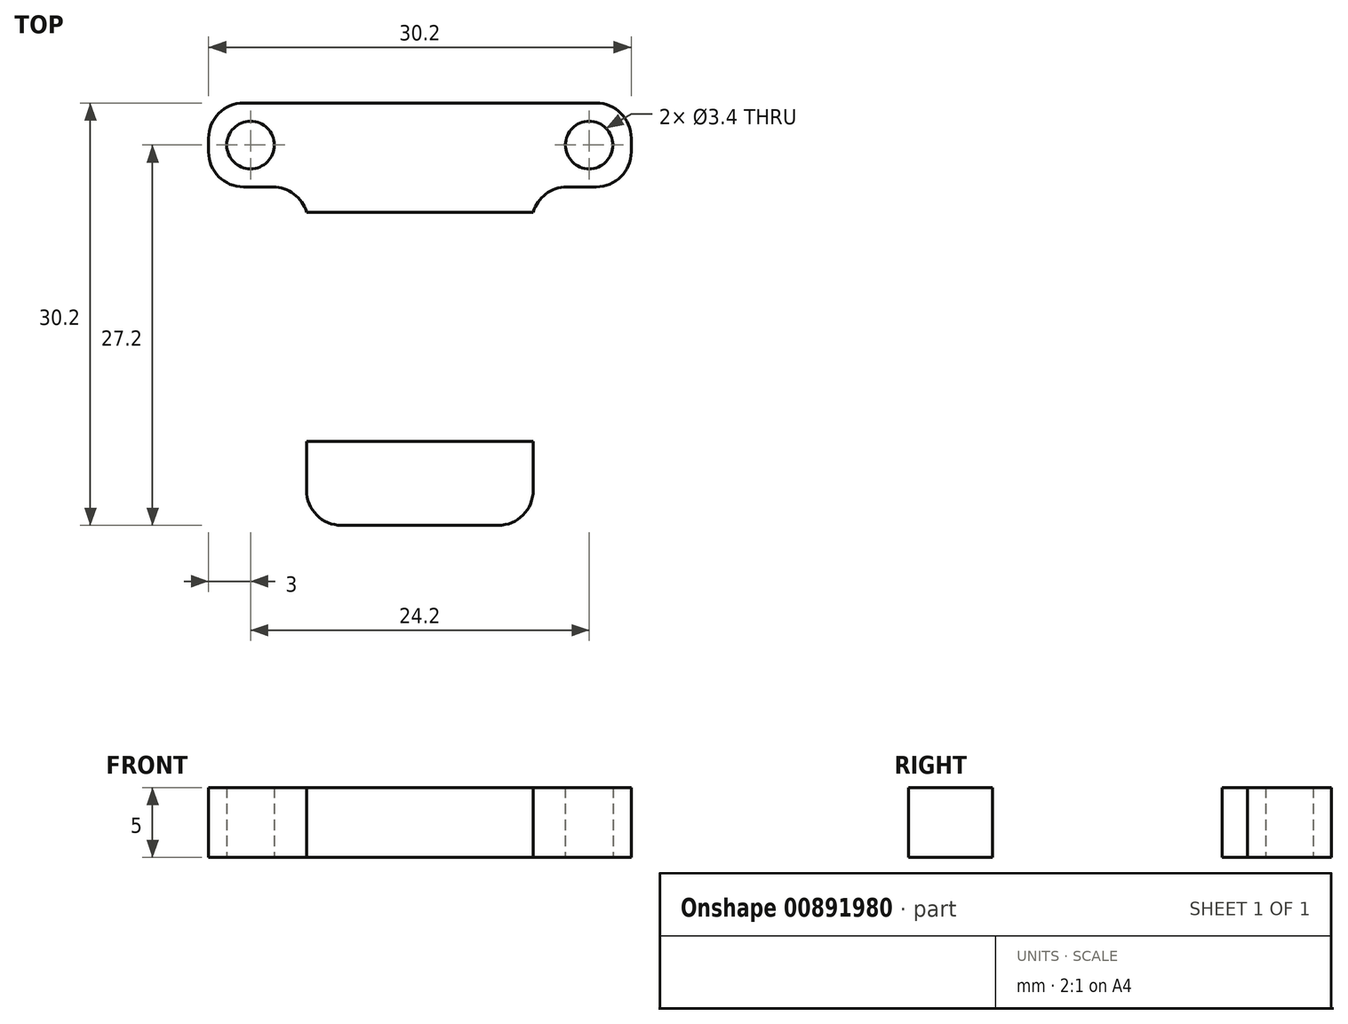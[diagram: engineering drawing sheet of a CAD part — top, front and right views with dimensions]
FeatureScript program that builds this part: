
annotation { "Feature Type Name" : "Feature", "Feature Type Description" : "" }
export const myFeature = defineFeature(function(context is Context, id is Id, definition is map)
    precondition{}
    {
        {
            var Q0;
            Q0=qCreatedBy(makeId("Top.planeOp"),FACE);
            var sketch = newSketch(context, id + "F0", { "sketchPlane" : qUnion([Q0])});
            skLineSegment(sketch, "E0.bottom", {"start": v(-15.1, -15.1) * mm, "end": v(15.1, -15.1) * mm});
            skLineSegment(sketch, "E0.top", {"start": v(-15.1, 15.1) * mm, "end": v(15.1, 15.1) * mm});
            skLineSegment(sketch, "E0.left", {"start": v(-15.1, -15.1) * mm, "end": v(-15.1, 15.1) * mm});
            skLineSegment(sketch, "E0.right", {"start": v(15.1, -15.1) * mm, "end": v(15.1, 15.1) * mm});
            skPoint(sketch, "E0.middle", {"position": v(0, 0) * mm});
            skLineSegment(sketch, "E1.bottom", {"start": v(-15.1, 15.1) * mm, "end": v(-12.1, 15.1) * mm});
            skLineSegment(sketch, "E1.top", {"start": v(-15.1, 12.1) * mm, "end": v(-12.1, 12.1) * mm, "construction": true});
            skLineSegment(sketch, "E1.left", {"start": v(-15.1, 15.1) * mm, "end": v(-15.1, 12.1) * mm});
            skLineSegment(sketch, "E1.right", {"start": v(-12.1, 15.1) * mm, "end": v(-12.1, 12.1) * mm, "construction": true});
            skLineSegment(sketch, "E2.1.0", {"start": v(-15.1, -12.1) * mm, "end": v(-12.1, -12.1) * mm, "construction": true});
            skLineSegment(sketch, "E2.1.1", {"start": v(-12.1, -15.1) * mm, "end": v(-12.1, -12.1) * mm, "construction": true});
            skLineSegment(sketch, "E2.1.2", {"start": v(-15.1, -15.1) * mm, "end": v(-15.1, -12.1) * mm});
            skLineSegment(sketch, "E2.2.0", {"start": v(12.1, -15.1) * mm, "end": v(12.1, -12.1) * mm, "construction": true});
            skLineSegment(sketch, "E2.2.1", {"start": v(15.1, -12.1) * mm, "end": v(12.1, -12.1) * mm, "construction": true});
            skLineSegment(sketch, "E2.2.2", {"start": v(15.1, -15.1) * mm, "end": v(12.1, -15.1) * mm});
            skLineSegment(sketch, "E2.3.0", {"start": v(15.1, 12.1) * mm, "end": v(12.1, 12.1) * mm, "construction": true});
            skLineSegment(sketch, "E2.3.1", {"start": v(12.1, 15.1) * mm, "end": v(12.1, 12.1) * mm, "construction": true});
            skLineSegment(sketch, "E2.3.2", {"start": v(15.1, 15.1) * mm, "end": v(15.1, 12.1) * mm});
            skLineSegment(sketch, "E3.bottom", {"start": v(-15.1, 15.1) * mm, "end": v(-9.1, 15.1) * mm});
            skLineSegment(sketch, "E3.top", {"start": v(-15.1, 9.1) * mm, "end": v(-9.1, 9.1) * mm, "construction": true});
            skLineSegment(sketch, "E3.left", {"start": v(-15.1, 15.1) * mm, "end": v(-15.1, 9.1) * mm});
            skLineSegment(sketch, "E3.right", {"start": v(-9.1, 15.1) * mm, "end": v(-9.1, 9.1) * mm, "construction": true});
            skLineSegment(sketch, "E4.1.0", {"start": v(-9.1, -15.1) * mm, "end": v(-9.1, -9.1) * mm, "construction": true});
            skLineSegment(sketch, "E4.1.1", {"start": v(-15.1, -9.1) * mm, "end": v(-9.1, -9.1) * mm, "construction": true});
            skLineSegment(sketch, "E4.2.0", {"start": v(15.1, -9.1) * mm, "end": v(9.1, -9.1) * mm, "construction": true});
            skLineSegment(sketch, "E4.2.1", {"start": v(9.1, -15.1) * mm, "end": v(9.1, -9.1) * mm, "construction": true});
            skLineSegment(sketch, "E4.3.0", {"start": v(9.1, 15.1) * mm, "end": v(9.1, 9.1) * mm, "construction": true});
            skLineSegment(sketch, "E4.3.1", {"start": v(15.1, 9.1) * mm, "end": v(9.1, 9.1) * mm, "construction": true});
            skLineSegment(sketch, "E5.bottom", {"start": v(-9.1, -9.1) * mm, "end": v(9.1, -9.1) * mm});
            skLineSegment(sketch, "E5.top", {"start": v(-9.1, 9.1) * mm, "end": v(9.1, 9.1) * mm});
            skLineSegment(sketch, "E5.left", {"start": v(-9.1, -9.1) * mm, "end": v(-9.1, 9.1) * mm});
            skLineSegment(sketch, "E5.right", {"start": v(9.1, -9.1) * mm, "end": v(9.1, 9.1) * mm});
            skLineSegment(sketch, "E6.bottom", {"start": v(-8.1, -15.1) * mm, "end": v(8.1, -15.1) * mm});
            skLineSegment(sketch, "E6.top", {"start": v(-8.1, -15.1) * mm, "end": v(8.1, -15.1) * mm});
            skLineSegment(sketch, "E6.left", {"start": v(-8.1, -15.1) * mm, "end": v(-8.1, -15.1) * mm});
            skLineSegment(sketch, "E6.right", {"start": v(8.1, -15.1) * mm, "end": v(8.1, -15.1) * mm});
            skPoint(sketch, "E6.middle", {"position": v(0, -15.1) * mm});
            skLineSegment(sketch, "E7.bottom", {"start": v(8.1, -15.1) * mm, "end": v(-8.1, -15.1) * mm});
            skLineSegment(sketch, "E7.top", {"start": v(8.1, 7.3) * mm, "end": v(-8.1, 7.3) * mm});
            skLineSegment(sketch, "E7.left", {"start": v(8.1, -15.1) * mm, "end": v(8.1, 7.3) * mm});
            skLineSegment(sketch, "E7.right", {"start": v(-8.1, -15.1) * mm, "end": v(-8.1, 7.3) * mm});
            skLineSegment(sketch, "E8.top", {"start": v(8.1, 9.1) * mm, "end": v(-8.1, 9.1) * mm});
            skLineSegment(sketch, "E8.left", {"start": v(8.1, 7.3) * mm, "end": v(8.1, 9.1) * mm});
            skLineSegment(sketch, "E8.right", {"start": v(-8.1, 7.3) * mm, "end": v(-8.1, 9.1) * mm});
            skLineSegment(sketch, "E9.bottom", {"start": v(9.1, 9.1) * mm, "end": v(15.1, 9.1) * mm});
            skLineSegment(sketch, "E9.top", {"start": v(9.1, -9.1) * mm, "end": v(15.1, -9.1) * mm});
            skLineSegment(sketch, "E9.left", {"start": v(9.1, 9.1) * mm, "end": v(9.1, -9.1) * mm});
            skLineSegment(sketch, "E9.right", {"start": v(15.1, 9.1) * mm, "end": v(15.1, -9.1) * mm});
            skLineSegment(sketch, "E10.bottom", {"start": v(-9.1, 9.1) * mm, "end": v(-15.1, 9.1) * mm});
            skLineSegment(sketch, "E10.top", {"start": v(-9.1, -9.1) * mm, "end": v(-15.1, -9.1) * mm});
            skLineSegment(sketch, "E10.left", {"start": v(-9.1, 9.1) * mm, "end": v(-9.1, -9.1) * mm});
            skLineSegment(sketch, "E10.right", {"start": v(-15.1, 9.1) * mm, "end": v(-15.1, -9.1) * mm});
            skSolve(sketch);
        }
        {
            var Q0;
            Q0=makeQuery(id+"F0.imprint","IMPRINT",FACE,{"disambiguationData":[TD([[makeQuery(id+"F0.imprint","IMPRINT",EDGE,{"derivedFrom":sQuery(id+"F0.wireOp",EDGE,"E0.bottom")}),1.0]])]});
            var Q1;
            Q1=makeQuery(id+"F0.imprint","IMPRINT",FACE,{"disambiguationData":[TD([[makeQuery(id+"F0.imprint","IMPRINT",EDGE,{"derivedFrom":sQuery(id+"F0.wireOp",EDGE,"E7.top")}),-1.0]])]});
            var Q2;
            {var subQ1=sQuery(id+"F0.wireOp",EDGE,"E0.top");Q2=makeQuery(id+"F0.imprint","IMPRINT",FACE,{"disambiguationData":[TD([[makeQuery(id+"F0.imprint","IMPRINT",EDGE,{"derivedFrom":subQ1}),-1.0]])]});}
            extrude(context, id + "F1", {"entities" : qUnion([Q0, Q1, Q2]), "depth" : 5 * mm, "offsetDistance" : 25 * mm});
        }
        {
            var Q0;
            Q0=sQuery(id+"F0.wireOp",VERTEX,"E2.1.0.end");
            var Q1;
            Q1=sQuery(id+"F0.wireOp",VERTEX,"E2.2.0.end");
            var Q2;
            Q2=makeQuery(id+"F1.opExtrude","SWEPT_BODY",BODY,{"disambiguationData":[OSD([sQuery(id+"F0.wireOp",EDGE,"E0.bottom"),sQuery(id+"F0.wireOp",EDGE,"E0.top"),sQuery(id+"F0.wireOp",EDGE,"E0.left"),sQuery(id+"F0.wireOp",EDGE,"E0.right"),sQuery(id+"F0.wireOp",EDGE,"E1.bottom"),sQuery(id+"F0.wireOp",EDGE,"E1.left"),sQuery(id+"F0.wireOp",EDGE,"E2.1.2"),sQuery(id+"F0.wireOp",EDGE,"E2.2.2"),sQuery(id+"F0.wireOp",EDGE,"E2.3.2")])]});
            hole(context, id + "F2", {"style" : HoleStyle.SIMPLE, "endStyle" : HoleEndStyle.THROUGH, "oppositeDirection" : true, "standardTappedOrClearance" : lookupTablePath({ "fit" : "Normal", "standard" : "ISO", "size" : "M3", "type" : "Clearance" }), "standardBlindInLast" : lookupTablePath({ "fit" : "Normal", "standard" : "ISO", "size" : "M3", "type" : "Clearance" }), "holeDiameter" : 3.4 * mm, "majorDiameter" : 5 * mm, "isTappedThrough" : true, "tappedDepth" : 12 * mm, "tapClearance" : 3, "locations" : qUnion([Q0, Q1]), "scope" : qUnion([Q2])});
        }
        {
            var Q0;
            Q0=makeQuery(id+"F1.opExtrude","SWEPT_EDGE",EDGE,{"disambiguationData":[OSD([sQuery(id+"F0.wireOp",EDGE,"E0.bottom"),sQuery(id+"F0.wireOp",EDGE,"E2.1.2")])]});
            var Q1;
            Q1=makeQuery(id+"F1.opExtrude","SWEPT_EDGE",EDGE,{"disambiguationData":[OSD([sQuery(id+"F0.wireOp",EDGE,"E0.right"),sQuery(id+"F0.wireOp",EDGE,"E2.2.2")])]});
            var Q2;
            Q2=makeQuery(id+"F1.opExtrude","SWEPT_EDGE",EDGE,{"disambiguationData":[OSD([sQuery(id+"F0.wireOp",EDGE,"E0.top"),sQuery(id+"F0.wireOp",EDGE,"E2.3.2")])]});
            var Q3;
            Q3=makeQuery(id+"F1.opExtrude","SWEPT_EDGE",EDGE,{"disambiguationData":[OSD([sQuery(id+"F0.wireOp",EDGE,"E3.bottom"),sQuery(id+"F0.wireOp",EDGE,"E3.left")])]});
            var Q4;
            Q4=makeQuery(id+"F1.opExtrude","SWEPT_EDGE",EDGE,{"disambiguationData":[OSD([sQuery(id+"F0.wireOp",EDGE,"E5.top"),sQuery(id+"F0.wireOp",EDGE,"E8.top"),sQuery(id+"F0.wireOp",EDGE,"E8.left")])]});
            var Q5;
            Q5=makeQuery(id+"F1.opExtrude","SWEPT_EDGE",EDGE,{"disambiguationData":[OSD([sQuery(id+"F0.wireOp",EDGE,"E5.top"),sQuery(id+"F0.wireOp",EDGE,"E8.top"),sQuery(id+"F0.wireOp",EDGE,"E8.right")])]});
            var Q6;
            Q6=makeQuery(id+"F1.opExtrude","SWEPT_EDGE",EDGE,{"disambiguationData":[OSD([sQuery(id+"F0.wireOp",EDGE,"E3.left"),sQuery(id+"F0.wireOp",EDGE,"E10.bottom"),sQuery(id+"F0.wireOp",EDGE,"E10.right")])]});
            var Q7;
            Q7=makeQuery(id+"F1.opExtrude","SWEPT_EDGE",EDGE,{"disambiguationData":[OSD([sQuery(id+"F0.wireOp",EDGE,"E0.right"),sQuery(id+"F0.wireOp",EDGE,"E9.bottom"),sQuery(id+"F0.wireOp",EDGE,"E9.right")])]});
            var Q8;
            Q8=makeQuery(id+"F1.opExtrude","SWEPT_EDGE",EDGE,{"disambiguationData":[OSD([sQuery(id+"F0.wireOp",EDGE,"E0.left"),sQuery(id+"F0.wireOp",EDGE,"E10.top"),sQuery(id+"F0.wireOp",EDGE,"E10.right")])]});
            var Q9;
            Q9=makeQuery(id+"F1.opExtrude","SWEPT_EDGE",EDGE,{"disambiguationData":[OSD([sQuery(id+"F0.wireOp",EDGE,"E0.right"),sQuery(id+"F0.wireOp",EDGE,"E9.top"),sQuery(id+"F0.wireOp",EDGE,"E9.right")])]});
            fillet(context, id + "F3", {"entities" : qUnion([Q0, Q1, Q2, Q3, Q4, Q5, Q6, Q7, Q8, Q9]), "radius" : 2.5 * mm, "tangentPropagation" : true, "allowEdgeOverflow" : false});
        }
        {
            var Q0;
            Q0=sQuery(id+"F0.wireOp",VERTEX,"E1.top.end");
            var Q1;
            Q1=sQuery(id+"F0.wireOp",VERTEX,"E2.3.0.end");
            var Q2;
            Q2=makeQuery(id+"F1.opExtrude","SWEPT_BODY",BODY,{"disambiguationData":[OSD([sQuery(id+"F0.wireOp",EDGE,"E0.top"),sQuery(id+"F0.wireOp",EDGE,"E0.right"),sQuery(id+"F0.wireOp",EDGE,"E2.3.2"),sQuery(id+"F0.wireOp",EDGE,"E3.bottom"),sQuery(id+"F0.wireOp",EDGE,"E3.left"),sQuery(id+"F0.wireOp",EDGE,"E5.top"),sQuery(id+"F0.wireOp",EDGE,"E7.top"),sQuery(id+"F0.wireOp",EDGE,"E8.left"),sQuery(id+"F0.wireOp",EDGE,"E8.right"),sQuery(id+"F0.wireOp",EDGE,"E9.bottom"),sQuery(id+"F0.wireOp",EDGE,"E10.bottom")])]});
            hole(context, id + "F4", {"style" : HoleStyle.SIMPLE, "endStyle" : HoleEndStyle.THROUGH, "oppositeDirection" : true, "standardTappedOrClearance" : lookupTablePath({ "fit" : "Normal", "standard" : "ISO", "size" : "M3", "type" : "Clearance" }), "standardBlindInLast" : lookupTablePath({ "fit" : "Normal", "standard" : "ISO", "size" : "M3", "type" : "Clearance" }), "holeDiameter" : 3.4 * mm, "majorDiameter" : 5 * mm, "isTappedThrough" : true, "tappedDepth" : 12 * mm, "tapClearance" : 3, "locations" : qUnion([Q0, Q1]), "scope" : qUnion([Q2])});
        }
    });
